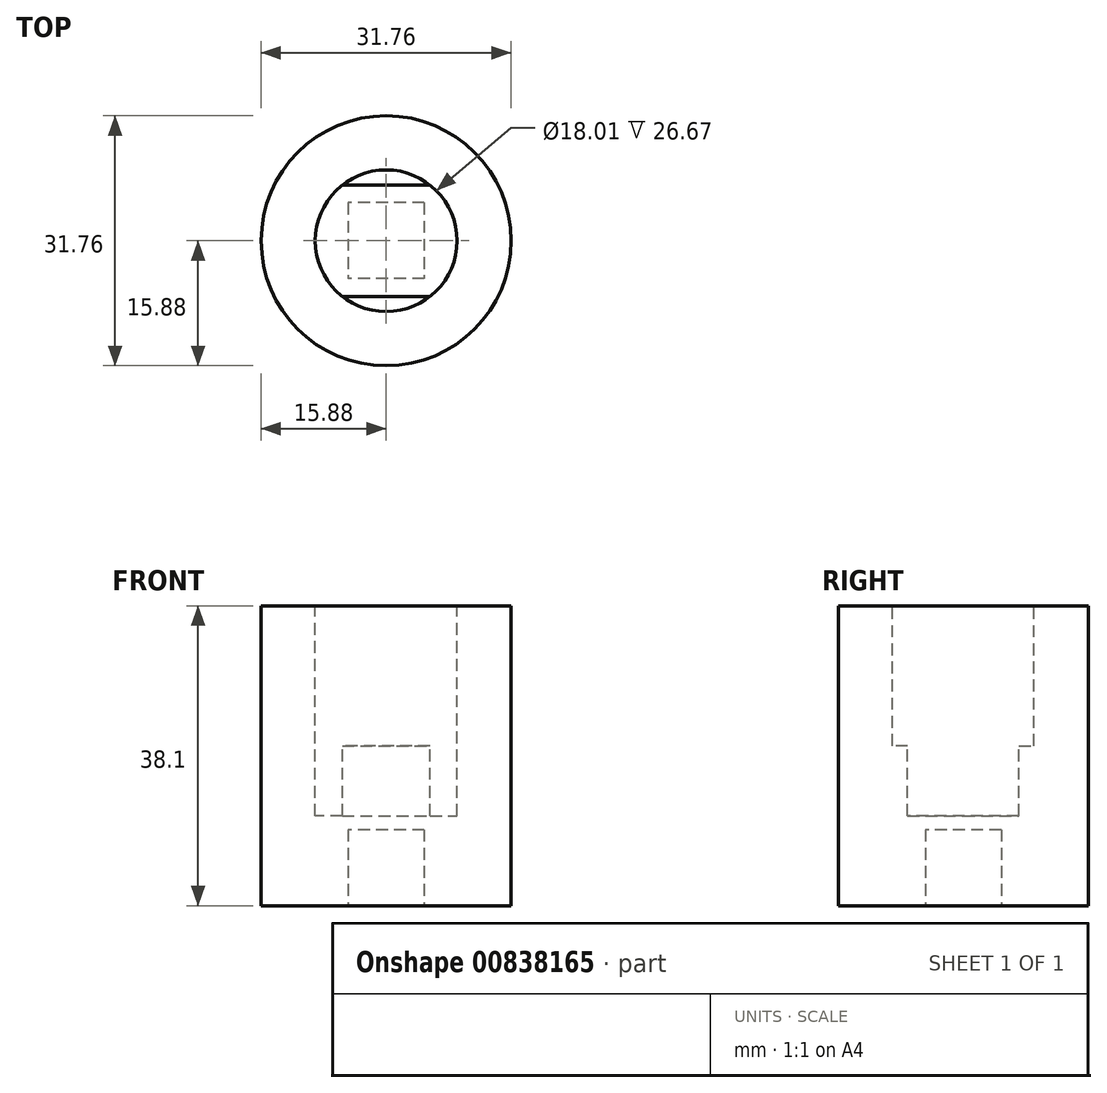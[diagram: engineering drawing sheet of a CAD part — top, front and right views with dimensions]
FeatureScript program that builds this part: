
annotation { "Feature Type Name" : "Feature", "Feature Type Description" : "" }
export const myFeature = defineFeature(function(context is Context, id is Id, definition is map)
    precondition{}
    {
        {
            var Q0;
            Q0=qCreatedBy(makeId("Top.planeOp"),FACE);
            var sketch = newSketch(context, id + "F0", { "sketchPlane" : qUnion([Q0])});
            skCircle(sketch, "E0", {"center": v(0, 0) * mm, "radius": 15.88 * mm});
            skSolve(sketch);
        }
        {
            var Q0;
            Q0=makeQuery(id+"F0.imprint","IMPRINT",FACE,{"disambiguationData":[TD([[makeQuery(id+"F0.imprint","IMPRINT",EDGE,{"derivedFrom":sQuery(id+"F0.wireOp",EDGE,"E0")}),1.0]])]});
            extrude(context, id + "F1", {"entities" : qUnion([Q0]), "oppositeDirection" : true, "depth" : 38.1 * mm, "offsetDistance" : 25.4 * mm});
        }
        {
            var Q0;
            Q0=makeQuery(id+"F1.opExtrude","CAP_FACE",FACE,{"disambiguationData":[OSD([sQuery(id+"F0.wireOp",EDGE,"E0")])],"isStart":false});
            var sketch = newSketch(context, id + "F2", { "sketchPlane" : qUnion([Q0])});
            skLineSegment(sketch, "E1.bottom", {"start": v(4.83, -4.83) * mm, "end": v(-4.83, -4.83) * mm});
            skLineSegment(sketch, "E1.top", {"start": v(4.83, 4.83) * mm, "end": v(-4.83, 4.83) * mm});
            skLineSegment(sketch, "E1.left", {"start": v(4.83, -4.83) * mm, "end": v(4.83, 4.83) * mm});
            skLineSegment(sketch, "E1.right", {"start": v(-4.83, -4.83) * mm, "end": v(-4.83, 4.83) * mm});
            skPoint(sketch, "E1.middle", {"position": v(0, 0) * mm});
            skSolve(sketch);
        }
        {
            var Q0;
            Q0=makeQuery(id+"F2.imprint","IMPRINT",FACE,{"disambiguationData":[TD([[makeQuery(id+"F2.imprint","IMPRINT",EDGE,{"derivedFrom":sQuery(id+"F2.wireOp",EDGE,"E1.bottom")}),-1.0]])]});
            extrude(context, id + "F3", {"entities" : qUnion([Q0]), "operationType" : NewBodyOperationType.REMOVE, "oppositeDirection" : true, "depth" : 9.65 * mm, "offsetDistance" : 25.4 * mm});
        }
        {
            var Q0;
            Q0=makeQuery(id+"F1.opExtrude","CAP_FACE",FACE,{"disambiguationData":[OSD([sQuery(id+"F0.wireOp",EDGE,"E0")])],"isStart":true});
            var sketch = newSketch(context, id + "F4", { "sketchPlane" : qUnion([Q0])});
            skCircle(sketch, "E2", {"center": v(0, 0) * mm, "radius": 9 * mm});
            skSolve(sketch);
        }
        {
            var Q0;
            Q0=makeQuery(id+"F4.imprint","IMPRINT",FACE,{"disambiguationData":[TD([[makeQuery(id+"F4.imprint","IMPRINT",EDGE,{"derivedFrom":sQuery(id+"F4.wireOp",EDGE,"E2")}),1.0]])]});
            extrude(context, id + "F5", {"entities" : qUnion([Q0]), "operationType" : NewBodyOperationType.REMOVE, "oppositeDirection" : true, "depth" : 17.78 * mm, "offsetDistance" : 25.4 * mm});
        }
        {
            var Q0;
            Q0=makeQuery(id+"F5.boolean.opBoolean","COPY",FACE,{"derivedFrom":makeQuery(id+"F5.opExtrude","CAP_FACE",FACE,{"disambiguationData":[OSD([sQuery(id+"F4.wireOp",EDGE,"E2")])],"isStart":false})});
            var sketch = newSketch(context, id + "F6", { "sketchPlane" : qUnion([Q0])});
            skPoint(sketch, "E3.middle", {"position": v(0, 0) * mm});
            skArc(sketch, "E4", {"start": v(-5.57, 7.07) * mm, "mid": v(-9, 0) * mm, "end": v(-5.57, -7.07) * mm});
            skLineSegment(sketch, "E5.bottom", {"start": v(-5.57, 7.07) * mm, "end": v(5.57, 7.07) * mm});
            skLineSegment(sketch, "E5.top", {"start": v(-5.57, -7.07) * mm, "end": v(5.57, -7.07) * mm});
            skPoint(sketch, "E6.orphan", {"position": v(-5.14, 7.07) * mm});
            skPoint(sketch, "E7.orphan", {"position": v(5.14, 7.07) * mm});
            skPoint(sketch, "E8.orphan", {"position": v(-5.14, -7.07) * mm});
            skPoint(sketch, "E9.orphan", {"position": v(5.14, -7.07) * mm});
            skArc(sketch, "E10.trimOffspring", {"start": v(5.57, -7.07) * mm, "mid": v(9, 0) * mm, "end": v(5.57, 7.07) * mm});
            skSolve(sketch);
        }
        {
            var Q0;
            Q0=makeQuery(id+"F6.imprint","IMPRINT",FACE,{"disambiguationData":[TD([[makeQuery(id+"F6.imprint","IMPRINT",EDGE,{"derivedFrom":sQuery(id+"F6.wireOp",EDGE,"E4")}),1.0]])]});
            extrude(context, id + "F7", {"entities" : qUnion([Q0]), "operationType" : NewBodyOperationType.REMOVE, "oppositeDirection" : true, "depth" : 8.9 * mm, "offsetDistance" : 25.4 * mm});
        }
    });
